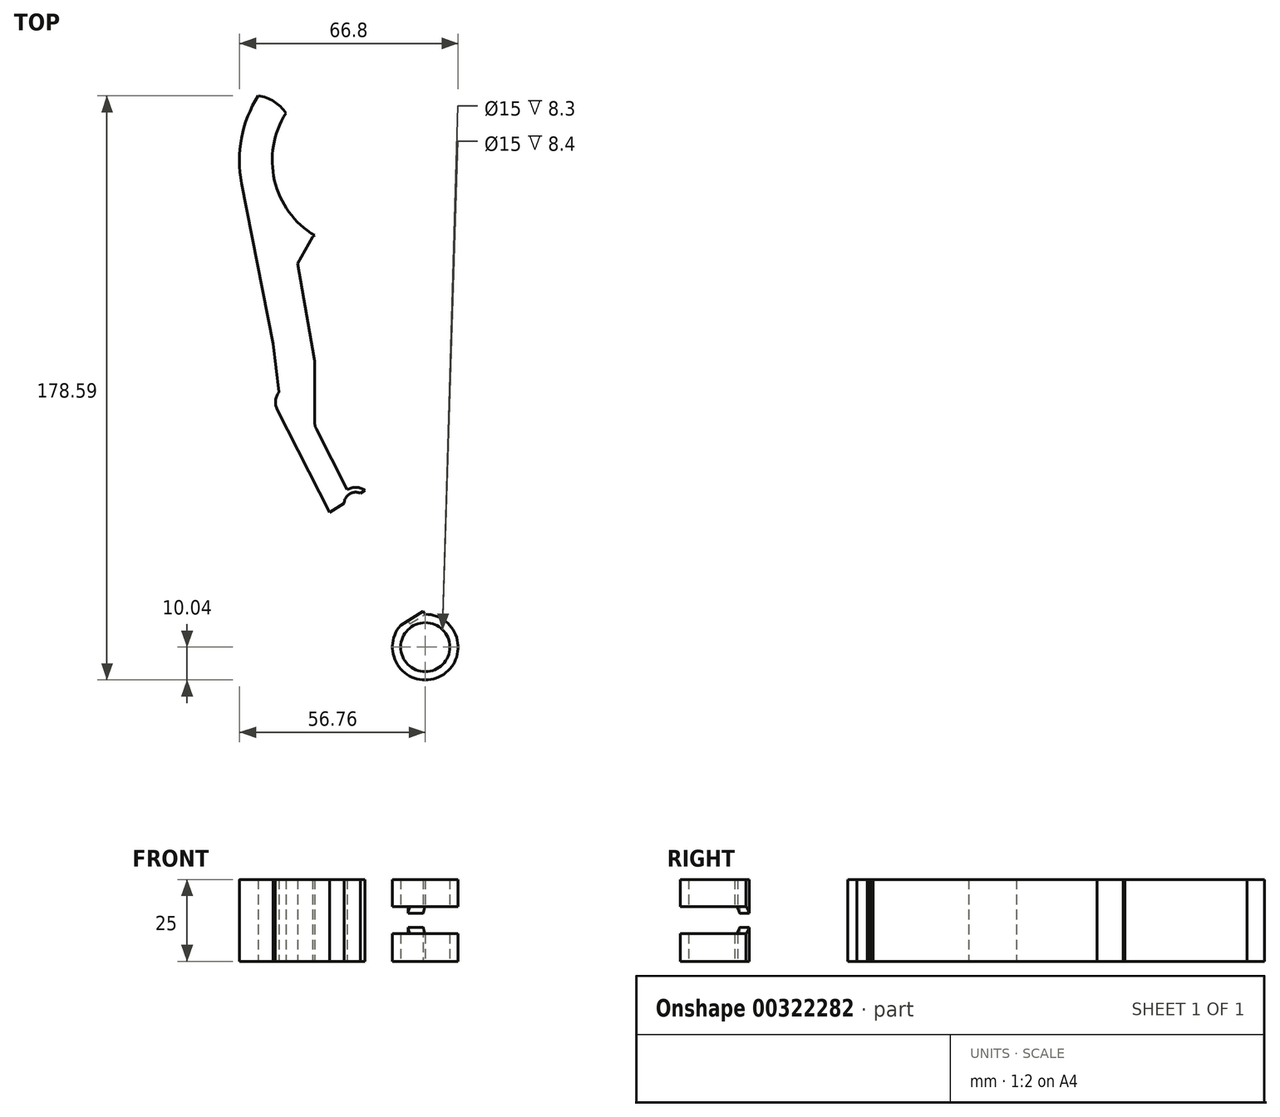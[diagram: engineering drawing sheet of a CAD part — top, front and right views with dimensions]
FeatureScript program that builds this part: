
annotation { "Feature Type Name" : "Feature", "Feature Type Description" : "" }
export const myFeature = defineFeature(function(context is Context, id is Id, definition is map)
    precondition{}
    {
        {
            var Q0;
            Q0=qCreatedBy(makeId("Top.planeOp"),FACE);
            var sketch = newSketch(context, id + "F0", { "sketchPlane" : qUnion([Q0])});
            skLineSegment(sketch, "E0", {"start": v(0, 0) * mm, "end": v(0, 10) * mm});
            skLineSegment(sketch, "E1", {"start": v(0, 10) * mm, "end": v(-23.85, 48.16) * mm});
            skLineSegment(sketch, "E2", {"start": v(-23.85, 48.16) * mm, "end": v(-46.55, 92.71) * mm});
            skLineSegment(sketch, "E3", {"start": v(-46.55, 92.71) * mm, "end": v(-56.09, 141.8) * mm});
            skLineSegment(sketch, "E4", {"start": v(0, 10) * mm, "end": v(0, 20.39) * mm});
            skLineSegment(sketch, "E5", {"start": v(0, 0) * mm, "end": v(-26.5, 42.4) * mm});
            skLineSegment(sketch, "E6", {"start": v(-26.5, 42.4) * mm, "end": v(-44.66, 78.04) * mm});
            skLineSegment(sketch, "E7", {"start": v(-44.66, 78.04) * mm, "end": v(-46.55, 92.71) * mm});
            skPoint(sketch, "E8", {"position": v(-33.83, 67.76) * mm});
            skLineSegment(sketch, "E9", {"start": v(-33.83, 67.76) * mm, "end": v(-33.83, 87.76) * mm});
            skLineSegment(sketch, "E10", {"start": v(-33.83, 87.76) * mm, "end": v(-39.04, 117.3) * mm});
            skLineSegment(sketch, "E11", {"start": v(-39.04, 117.3) * mm, "end": v(-34.04, 125.97) * mm});
            skArc(sketch, "E12", {"start": v(-56.09, 141.8) * mm, "mid": v(-50.15, 127.75) * mm, "end": v(-39.04, 117.3) * mm});
            skArc(sketch, "E13.0", {"start": v(-46.27, 143.7) * mm, "mid": v(-41.94, 133.47) * mm, "end": v(-33.85, 125.85) * mm});
            skArc(sketch, "E14", {"start": v(-33.85, 125.85) * mm, "mid": v(-46.05, 142.7) * mm, "end": v(-42.6, 163.2) * mm});
            skArc(sketch, "E15.0", {"start": v(-39.04, 117.3) * mm, "mid": v(-55.8, 140.41) * mm, "end": v(-51.06, 168.55) * mm});
            skArc(sketch, "E16", {"start": v(-42.6, 163.2) * mm, "mid": v(-46.23, 166.83) * mm, "end": v(-51.06, 168.55) * mm});
            skArc(sketch, "E17", {"start": v(-42.6, 163.2) * mm, "mid": v(-46.1, 142.68) * mm, "end": v(-33.85, 125.85) * mm});
            skArc(sketch, "E18", {"start": v(-33.85, 125.85) * mm, "mid": v(-37.1, 121.98) * mm, "end": v(-39.04, 117.3) * mm});
            skPoint(sketch, "E19", {"position": v(-21.2, 43.92) * mm});
            skPoint(sketch, "E20", {"position": v(-18.55, 39.68) * mm});
            skPoint(sketch, "E21", {"position": v(-23.85, 48.16) * mm});
            skArc(sketch, "E22", {"start": v(-18.55, 39.68) * mm, "mid": v(-17.04, 46.52) * mm, "end": v(-23.85, 48.16) * mm});
            skSolve(sketch);
        }
        {
            var Q0;
            {var subQ1=sQuery(id+"F0.wireOp",EDGE,"E3");Q0=makeQuery(id+"F0.imprint","IMPRINT",FACE,{"disambiguationData":[TD([[makeQuery(id+"F0.imprint","IMPRINT",EDGE,{"derivedFrom":subQ1}),-1.0]])]});}
            var Q1;
            Q1=makeQuery(id+"F0.imprint","IMPRINT",FACE,{"disambiguationData":[TD([[makeQuery(id+"F0.imprint","IMPRINT",EDGE,{"derivedFrom":sQuery(id+"F0.wireOp",EDGE,"E0")}),1.0]])]});
            extrude(context, id + "F1", {"entities" : qUnion([Q0, Q1]), "depth" : 25 * mm});
        }
        {
            var Q0;
            Q0 = qSketchRegion(id + "F0", true);
            extrude(context, id + "F2", {"entities" : qUnion([Q0]), "operationType" : NewBodyOperationType.ADD, "depth" : 25 * mm});
        }
        {
            var Q0;
            Q0=qCreatedBy(makeId("Top.planeOp"),FACE);
            var sketch = newSketch(context, id + "F3", { "sketchPlane" : qUnion([Q0])});
            skCircle(sketch, "E23", {"center": v(0, 0) * mm, "radius": 10.04 * mm});
            skSolve(sketch);
        }
        {
            var Q0;
            Q0=makeQuery(id+"F3.imprint","IMPRINT",FACE,{"disambiguationData":[TD([[makeQuery(id+"F3.imprint","IMPRINT",EDGE,{"derivedFrom":sQuery(id+"F3.wireOp",EDGE,"E23")}),1.0]])]});
            extrude(context, id + "F4", {"entities" : qUnion([Q0]), "operationType" : NewBodyOperationType.ADD, "depth" : 25 * mm});
        }
        {
            var Q0;
            Q0=makeQuery(id+"F1.opExtrude","SWEPT_FACE",FACE,{"disambiguationData":[OSD([sQuery(id+"F0.wireOp",EDGE,"E5")])]});
            var sketch = newSketch(context, id + "F5", { "sketchPlane" : qUnion([Q0])});
            skPoint(sketch, "E24", {"position": v(-10.04, 16.7) * mm});
            skPoint(sketch, "E25", {"position": v(-10.04, 8.4) * mm});
            skLineSegment(sketch, "E26.bottom", {"start": v(-10.04, 16.7) * mm, "end": v(-15.57, 16.7) * mm});
            skLineSegment(sketch, "E26.top", {"start": v(-10.04, 8.4) * mm, "end": v(-15.57, 8.4) * mm});
            skLineSegment(sketch, "E26.left", {"start": v(-10.04, 16.7) * mm, "end": v(-10.04, 8.4) * mm});
            skLineSegment(sketch, "E26.right", {"start": v(-15.57, 16.7) * mm, "end": v(-15.57, 8.4) * mm});
            skSolve(sketch);
        }
        {
            var Q0;
            Q0=makeQuery(id+"F5.imprint","IMPRINT",FACE,{"disambiguationData":[TD([[makeQuery(id+"F5.imprint","IMPRINT",EDGE,{"derivedFrom":sQuery(id+"F5.wireOp",EDGE,"E26.bottom")}),1.0]])]});
            extrude(context, id + "F6", {"entities" : qUnion([Q0]), "operationType" : NewBodyOperationType.ADD, "depth" : 25 * mm});
        }
        {
            var Q0;
            Q0=makeQuery(id+"F6.opExtrude","SWEPT_FACE",FACE,{"disambiguationData":[OSD([sQuery(id+"F5.wireOp",EDGE,"E26.left")])]});
            extrude(context, id + "F7", {"entities" : qUnion([Q0]), "operationType" : NewBodyOperationType.REMOVE, "depth" : 54.1 * mm});
        }
        {
            var Q0;
            Q0=makeQuery(id+"F6.opExtrude","SWEPT_FACE",FACE,{"disambiguationData":[OSD([sQuery(id+"F5.wireOp",EDGE,"E26.left")])]});
            extrude(context, id + "F8", {"entities" : qUnion([Q0]), "operationType" : NewBodyOperationType.REMOVE, "endBound" : BoundingType.SYMMETRIC, "depth" : 84 * mm});
        }
        {
            var Q0;
            {var subQ0=sQuery(id+"F5.wireOp",EDGE,"E26.left");var subQ1=sQuery(id+"F3.wireOp",EDGE,"E23");var subQ2=sQuery(id+"F0.wireOp",EDGE,"E5");Q0=makeQuery(id+"F8.boolean.opBoolean","MERGE",FACE,{"derivedFrom":[makeQuery(id+"F1.opExtrude","SWEPT_FACE",FACE,{"disambiguationData":[OSD([subQ2])]}),makeQuery(id+"F7.boolean.opBoolean","COPY",FACE,{"derivedFrom":makeQuery(id+"F7.opExtrude","SWEPT_FACE",FACE,{"disambiguationData":[OSD([subQ2,subQ1,subQ0])]})}),makeQuery(id+"F8.opExtrude","SWEPT_FACE",FACE,{"disambiguationData":[OSD([subQ2,subQ1,subQ0])]})]});}
            var sketch = newSketch(context, id + "F9", { "sketchPlane" : qUnion([Q0])});
            skLineSegment(sketch, "E27.bottom", {"start": v(10.04, 16.7) * mm, "end": v(-10.04, 16.7) * mm});
            skLineSegment(sketch, "E27.top", {"start": v(10.04, 8.4) * mm, "end": v(-10.04, 8.4) * mm});
            skLineSegment(sketch, "E27.left", {"start": v(10.04, 16.7) * mm, "end": v(10.04, 8.4) * mm});
            skLineSegment(sketch, "E27.right", {"start": v(-10.04, 16.7) * mm, "end": v(-10.04, 8.4) * mm});
            skSolve(sketch);
        }
        {
            var Q0;
            Q0=makeQuery(id+"F9.imprint","IMPRINT",FACE,{"disambiguationData":[TD([[makeQuery(id+"F9.imprint","IMPRINT",EDGE,{"derivedFrom":sQuery(id+"F9.wireOp",EDGE,"E27.bottom")}),1.0]])]});
            extrude(context, id + "F10", {"entities" : qUnion([Q0]), "operationType" : NewBodyOperationType.REMOVE, "oppositeDirection" : true, "depth" : 25 * mm});
        }
        {
            var Q0;
            {var subQ0=sQuery(id+"F0.wireOp",EDGE,"E15.0");var subQ1=sQuery(id+"F0.wireOp",EDGE,"E10");var subQ2=sQuery(id+"F0.wireOp",EDGE,"E9");var subQ3=sQuery(id+"F0.wireOp",EDGE,"E7");var subQ4=sQuery(id+"F0.wireOp",EDGE,"E6");var subQ5=sQuery(id+"F0.wireOp",EDGE,"E5");var subQ6=sQuery(id+"F0.wireOp",EDGE,"E3");var subQ7=sQuery(id+"F0.wireOp",EDGE,"E2");var subQ8=sQuery(id+"F0.wireOp",EDGE,"E1");var subQ9=sQuery(id+"F0.wireOp",EDGE,"E0");Q0=makeQuery(id+"F4.boolean.opBoolean","MERGE",FACE,{"derivedFrom":[makeQuery(id+"F2.boolean.opBoolean","MERGE",FACE,{"derivedFrom":[makeQuery(id+"F1.opExtrude","CAP_FACE",FACE,{"disambiguationData":[OSD([subQ9,subQ8,subQ7,subQ6,subQ5,subQ4,subQ3,subQ2,subQ1,subQ0])],"isStart":true}),makeQuery(id+"F2.opExtrude","CAP_FACE",FACE,{"disambiguationData":[OSD([subQ9,subQ8,subQ7,subQ6,subQ5,subQ4,subQ3,subQ2,subQ1,sQuery(id+"F0.wireOp",EDGE,"E11"),sQuery(id+"F0.wireOp",EDGE,"E14"),subQ0,sQuery(id+"F0.wireOp",EDGE,"E16"),sQuery(id+"F0.wireOp",EDGE,"E18")])],"isStart":true})]}),makeQuery(id+"F4.opExtrude","CAP_FACE",FACE,{"disambiguationData":[OSD([sQuery(id+"F3.wireOp",EDGE,"E23")])],"isStart":true})]});}
            var sketch = newSketch(context, id + "F11", { "sketchPlane" : qUnion([Q0])});
            skCircle(sketch, "E28", {"center": v(0, 0) * mm, "radius": 8.63 * mm});
            skLineSegment(sketch, "E29", {"start": v(-5.45, 6.7) * mm, "end": v(0, 0) * mm});
            skLineSegment(sketch, "E30", {"start": v(-5.45, 6.7) * mm, "end": v(5.45, -6.7) * mm});
            skSolve(sketch);
        }
        {
            var Q0;
            Q0=sQuery(id+"F11.wireOp",VERTEX,"E28.center");
            var Q1;
            Q1=makeQuery(id+"F1.opExtrude","SWEPT_BODY",BODY,{"disambiguationData":[OSD([sQuery(id+"F0.wireOp",EDGE,"E0"),sQuery(id+"F0.wireOp",EDGE,"E1"),sQuery(id+"F0.wireOp",EDGE,"E2"),sQuery(id+"F0.wireOp",EDGE,"E3"),sQuery(id+"F0.wireOp",EDGE,"E5"),sQuery(id+"F0.wireOp",EDGE,"E6"),sQuery(id+"F0.wireOp",EDGE,"E7"),sQuery(id+"F0.wireOp",EDGE,"E9"),sQuery(id+"F0.wireOp",EDGE,"E10"),sQuery(id+"F0.wireOp",EDGE,"E15.0")])]});
            hole(context, id + "F12", {"style" : HoleStyle.SIMPLE, "endStyle" : HoleEndStyle.THROUGH, "holeDiameter" : 15 * mm, "tappedDepth" : 12 * mm, "tapClearance" : 3, "locations" : qUnion([Q0]), "scope" : qUnion([Q1])});
        }
        {
            var Q0;
            Q0=makeQuery(id+"F1.opExtrude","SWEPT_FACE",FACE,{"disambiguationData":[OSD([sQuery(id+"F0.wireOp",EDGE,"E1")])]});
            var sketch = newSketch(context, id + "F13", { "sketchPlane" : qUnion([Q0])});
            skArc(sketch, "E31", {"start": v(8.52, 8.4) * mm, "mid": v(9.97, 12.55) * mm, "end": v(8.52, 16.7) * mm});
            skSolve(sketch);
        }
        {
            var Q0;
            Q0 = qSketchRegion(id + "F13", true);
            var Q1;
            Q1=makeQuery(id+"F13.imprint","IMPRINT",FACE,{"disambiguationData":[TD([[makeQuery(id+"F13.imprint","IMPRINT",EDGE,{"derivedFrom":sQuery(id+"F13.wireOp",EDGE,"E31")}),-1.0]])]});
            extrude(context, id + "F14", {"entities" : qUnion([Q0, Q1]), "operationType" : NewBodyOperationType.ADD, "oppositeDirection" : true, "depth" : 5.5 * mm});
        }
        {
            var Q0;
            {var subQ0=sQuery(id+"F5.wireOp",EDGE,"E26.left");var subQ1=sQuery(id+"F3.wireOp",EDGE,"E23");var subQ2=sQuery(id+"F0.wireOp",EDGE,"E5");Q0=makeQuery(id+"F8.boolean.opBoolean","MERGE",FACE,{"derivedFrom":[makeQuery(id+"F1.opExtrude","SWEPT_FACE",FACE,{"disambiguationData":[OSD([subQ2])]}),makeQuery(id+"F7.boolean.opBoolean","COPY",FACE,{"derivedFrom":makeQuery(id+"F7.opExtrude","SWEPT_FACE",FACE,{"disambiguationData":[OSD([subQ2,subQ1,subQ0])]})}),makeQuery(id+"F8.opExtrude","SWEPT_FACE",FACE,{"disambiguationData":[OSD([subQ2,subQ1,subQ0])]})]});}
            extrude(context, id + "F15", {"entities" : qUnion([Q0]), "operationType" : NewBodyOperationType.ADD, "depth" : 3 * mm});
        }
        {
            var Q0;
            Q0=makeQuery(id+"F1.opExtrude","SWEPT_FACE",FACE,{"disambiguationData":[OSD([sQuery(id+"F0.wireOp",EDGE,"E6")])]});
            extrude(context, id + "F16", {"entities" : qUnion([Q0]), "operationType" : NewBodyOperationType.ADD, "depth" : 3 * mm});
        }
        {
            var Q0;
            Q0=makeQuery(id+"F15.opExtrude","SWEPT_FACE",FACE,{"disambiguationData":[OSD([sQuery(id+"F0.wireOp",EDGE,"E5"),sQuery(id+"F0.wireOp",EDGE,"E6")])]});
            extrude(context, id + "F17", {"entities" : qUnion([Q0]), "operationType" : NewBodyOperationType.ADD, "depth" : 0.39 * mm});
        }
        {
            var Q0;
            Q0=makeQuery(id+"F15.opExtrude","SWEPT_FACE",FACE,{"disambiguationData":[OSD([sQuery(id+"F0.wireOp",EDGE,"E5"),sQuery(id+"F3.wireOp",EDGE,"E23"),sQuery(id+"F9.wireOp",EDGE,"E27.right")])]});
            extrude(context, id + "F18", {"entities" : qUnion([Q0]), "operationType" : NewBodyOperationType.ADD, "depth" : 0.43 * mm});
        }
        {
            var Q0;
            Q0=makeQuery(id+"F18.opExtrude","SWEPT_FACE",FACE,{"disambiguationData":[OSD([sQuery(id+"F0.wireOp",EDGE,"E1"),sQuery(id+"F9.wireOp",EDGE,"E27.right")])]});
            extrude(context, id + "F19", {"entities" : qUnion([Q0]), "operationType" : NewBodyOperationType.REMOVE, "oppositeDirection" : true, "depth" : 25 * mm});
        }
        {
            var Q0;
            {var subQ0=sQuery(id+"F0.wireOp",EDGE,"E7");var subQ1=sQuery(id+"F0.wireOp",EDGE,"E6");Q0=makeQuery(id+"FcaMvRAIBmcSUP5_1.boolean.opBoolean","MERGE",EDGE,{"derivedFrom":[makeQuery(id+"F16.opExtrude","CAP_EDGE",EDGE,{"disambiguationData":[OSD([subQ1,subQ0])],"isStart":false}),makeQuery(id+"FcaMvRAIBmcSUP5_1.opExtrude","SWEPT_EDGE",EDGE,{"disambiguationData":[OSD([subQ1,subQ0,sQuery(id+"FYqlTbUe4as9PVL_1.wireOp",EDGE,"Du2J6gcl-uKUM-Kpxn-wIgO-H1HJFY8qbqDL")])]})]});}
            fillet(context, id + "F20", {"entities" : qUnion([Q0]), "radius" : 5 * mm, "tangentPropagation" : true, "allowEdgeOverflow" : false});
        }
        {
            var Q0;
            Q0=makeQuery(id+"F1.opExtrude","SWEPT_EDGE",EDGE,{"disambiguationData":[OSD([sQuery(id+"F0.wireOp",EDGE,"E2"),sQuery(id+"F0.wireOp",EDGE,"E9")])]});
            fillet(context, id + "F21", {"entities" : qUnion([Q0]), "radius" : 5 * mm, "tangentPropagation" : true, "allowEdgeOverflow" : false});
        }
        {
            var Q0;
            Q0=makeQuery(id+"F1.opExtrude","SWEPT_EDGE",EDGE,{"disambiguationData":[OSD([sQuery(id+"F0.wireOp",EDGE,"E9"),sQuery(id+"F0.wireOp",EDGE,"E10")])]});
            fillet(context, id + "F22", {"entities" : qUnion([Q0]), "radius" : 5 * mm, "tangentPropagation" : true, "allowEdgeOverflow" : false});
        }
        {
            var Q0;
            {var subQ0=sQuery(id+"F3.wireOp",EDGE,"E23");var subQ1=sQuery(id+"F0.wireOp",EDGE,"E5");var subQ2=sQuery(id+"F0.wireOp",EDGE,"E6");var subQ3=sQuery(id+"F0.wireOp",EDGE,"E15.0");var subQ4=sQuery(id+"F0.wireOp",EDGE,"E10");var subQ5=sQuery(id+"F0.wireOp",EDGE,"E9");var subQ6=sQuery(id+"F0.wireOp",EDGE,"E7");var subQ7=sQuery(id+"F0.wireOp",EDGE,"E3");var subQ8=sQuery(id+"F0.wireOp",EDGE,"E2");var subQ9=sQuery(id+"F0.wireOp",EDGE,"E1");var subQ10=sQuery(id+"F0.wireOp",EDGE,"E0");Q0=makeQuery(id+"F18.boolean.opBoolean","MERGE",FACE,{"derivedFrom":[makeQuery(id+"F17.boolean.opBoolean","MERGE",FACE,{"derivedFrom":[makeQuery(id+"F16.boolean.opBoolean","MERGE",FACE,{"derivedFrom":[makeQuery(id+"F15.boolean.opBoolean","MERGE",FACE,{"derivedFrom":[makeQuery(id+"F4.boolean.opBoolean","MERGE",FACE,{"derivedFrom":[makeQuery(id+"F2.boolean.opBoolean","MERGE",FACE,{"derivedFrom":[makeQuery(id+"F1.opExtrude","CAP_FACE",FACE,{"disambiguationData":[OSD([subQ10,subQ9,subQ8,subQ7,subQ1,subQ2,subQ6,subQ5,subQ4,subQ3])],"isStart":true}),makeQuery(id+"F2.opExtrude","CAP_FACE",FACE,{"disambiguationData":[OSD([subQ10,subQ9,subQ8,subQ7,subQ1,subQ2,subQ6,subQ5,subQ4,sQuery(id+"F0.wireOp",EDGE,"E11"),sQuery(id+"F0.wireOp",EDGE,"E14"),subQ3,sQuery(id+"F0.wireOp",EDGE,"E16"),sQuery(id+"F0.wireOp",EDGE,"E18"),sQuery(id+"F0.wireOp",EDGE,"E22")])],"isStart":true})]}),makeQuery(id+"F4.opExtrude","CAP_FACE",FACE,{"disambiguationData":[OSD([subQ0])],"isStart":true})]}),makeQuery(id+"F15.opExtrude","SWEPT_FACE",FACE,{"disambiguationData":[OSD([subQ1]),TDD([makeQuery(id+"F1.opExtrude","CAP_EDGE",EDGE,{"disambiguationData":[OSD([subQ1])],"isStart":true})])]})]}),makeQuery(id+"F16.opExtrude","SWEPT_FACE",FACE,{"disambiguationData":[OSD([subQ2]),TDD([makeQuery(id+"F1.opExtrude","CAP_EDGE",EDGE,{"disambiguationData":[OSD([subQ2])],"isStart":true})])]})]}),makeQuery(id+"F17.opExtrude","SWEPT_FACE",FACE,{"disambiguationData":[OSD([subQ1,subQ2]),TDD([makeQuery(id+"F15.opExtrude","SWEPT_EDGE",EDGE,{"disambiguationData":[OSD([subQ1,subQ2]),TDD([makeQuery(id+"F1.opExtrude","CAP_VERTEX",VERTEX,{"disambiguationData":[OSD([subQ1,subQ2])],"isStart":true})])]})])]})]}),makeQuery(id+"F18.opExtrude","SWEPT_FACE",FACE,{"disambiguationData":[OSD([subQ1,subQ0]),TDD([makeQuery(id+"F15.opExtrude","SWEPT_EDGE",EDGE,{"disambiguationData":[OSD([subQ1,subQ0]),TDD([makeQuery(id+"F4.boolean.opBoolean","INTERSECT",VERTEX,{"disambiguationData":[OD(0.0)],"derivedFrom":[makeQuery(id+"F1.opExtrude","SWEPT_FACE",FACE,{"disambiguationData":[OSD([subQ1])]}),makeQuery(id+"F4.opExtrude","SWEPT_FACE",FACE,{"disambiguationData":[OSD([subQ0])]})]})])]})])]})]});}
            var sketch = newSketch(context, id + "F23", { "sketchPlane" : qUnion([Q0])});
            skPoint(sketch, "E32", {"position": v(-21.29, -43.87) * mm});
            skCircle(sketch, "E33", {"center": v(-21.29, -43.87) * mm, "radius": 3.5 * mm});
            skSolve(sketch);
        }
        {
            var Q0;
            Q0 = qSketchRegion(id + "F23", true);
            extrude(context, id + "F24", {"entities" : qUnion([Q0]), "operationType" : NewBodyOperationType.REMOVE, "oppositeDirection" : true, "depth" : 25 * mm});
        }
    });
